# Revit family: CE
name_source: partatom
category: Lighting Fixtures
revit_build: Autodesk Revit MEP 2012 (Build: 20110309_2315(x64)
units: mm (PartAtom-declared; Revit-internal decimal feet)

## types (7) — shared parameters
Color Filter = 16777215
Default Elevation = 48.000"
Dimming Lamp Color Temperature Shift = <None>
Emit Shape Visible in Rendering = No
Emit from Rectangle Length = 10.000"
Emit from Rectangle Width = 5.000"
Is 120VAC = Yes
Is 277VAC = No
Lamp = LED Lamp
Load Classification = Lighting
Manufacturer = Compass Lighting
Manufacturer Fax = 866-898-0131
Photometric Web File = generic
Product Documentation Link = http://cdn.compasslightingproducts.com
Product Page URL = http://www.compasslightingproducts.com
Tilt Angle = 0.00°
URL = http://www.compasslightingproducts.com
Voltage = 120 V
zz Watts 1 = 1 W
zz Watts 2 = 2 W
zz Watts 3 = 4 W
zz Watts 4 = 3 W

## per-type parameters (varying)
| type | Apparent Load | Description | Finish | Lens | Wattage Comments | Watts | zz Integer 1 |
| CER | 2 VA | White Thermoplastic Exit, Universal Face, Red LED Emergency Exit | Hubbell - White | Hubbell - Red Glass | 1.78 - 1.88 W | 2 W | 2 |
| CERB | 2 VA | Black Thermoplastic Exit, Universal Face, Red LED Emergency Exit | Hubbell - Black | Hubbell - Red Glass | 1.78 - 1.88 W | 2 W | 2 |
| CEG | 1 VA | White Thermoplastic Exit, Universal Face, Green LED Emergency Exit | Hubbell - White | Hubbell - Green Glass | 1.49 - 1.57 W | 1 W | 1 |
| CEGB | 1 VA | Black Thermoplastic Exit, Universal Face, Green LED Emergency Exit | Hubbell - Black | Hubbell - Green Glass | 1.49 - 1.57 W | 1 W | 1 |
| CERRC | 4 VA | White Thermoplastic Exit, Universal Face, Red LED Emergency Exit,Remote Capacity | Hubbell - White | Hubbell - Red Glass | 3.6 - 4.14 W | 4 W | 3 |
| CERRCB | 4 VA | Black Thermoplastic Exit, Universal Face, Red LED Emergency Exit,Remote Capacity | Hubbell - Black | Hubbell - Red Glass | 3.6 - 4.14 W | 4 W | 3 |
| CEGRC | 3 VA | White Thermoplastic Exit, Universal Face, Green LED Emergency Exit, Remote Capacity | Hubbell - White | Hubbell - Green Glass | 3.28 - 3.81 W | 3 W | 4 |

note: column(s) folded — value = type name in every type: Model

## geometry (parser evidence)
native form markers: Sweep x1
no freeform markers — native parametric forms only
